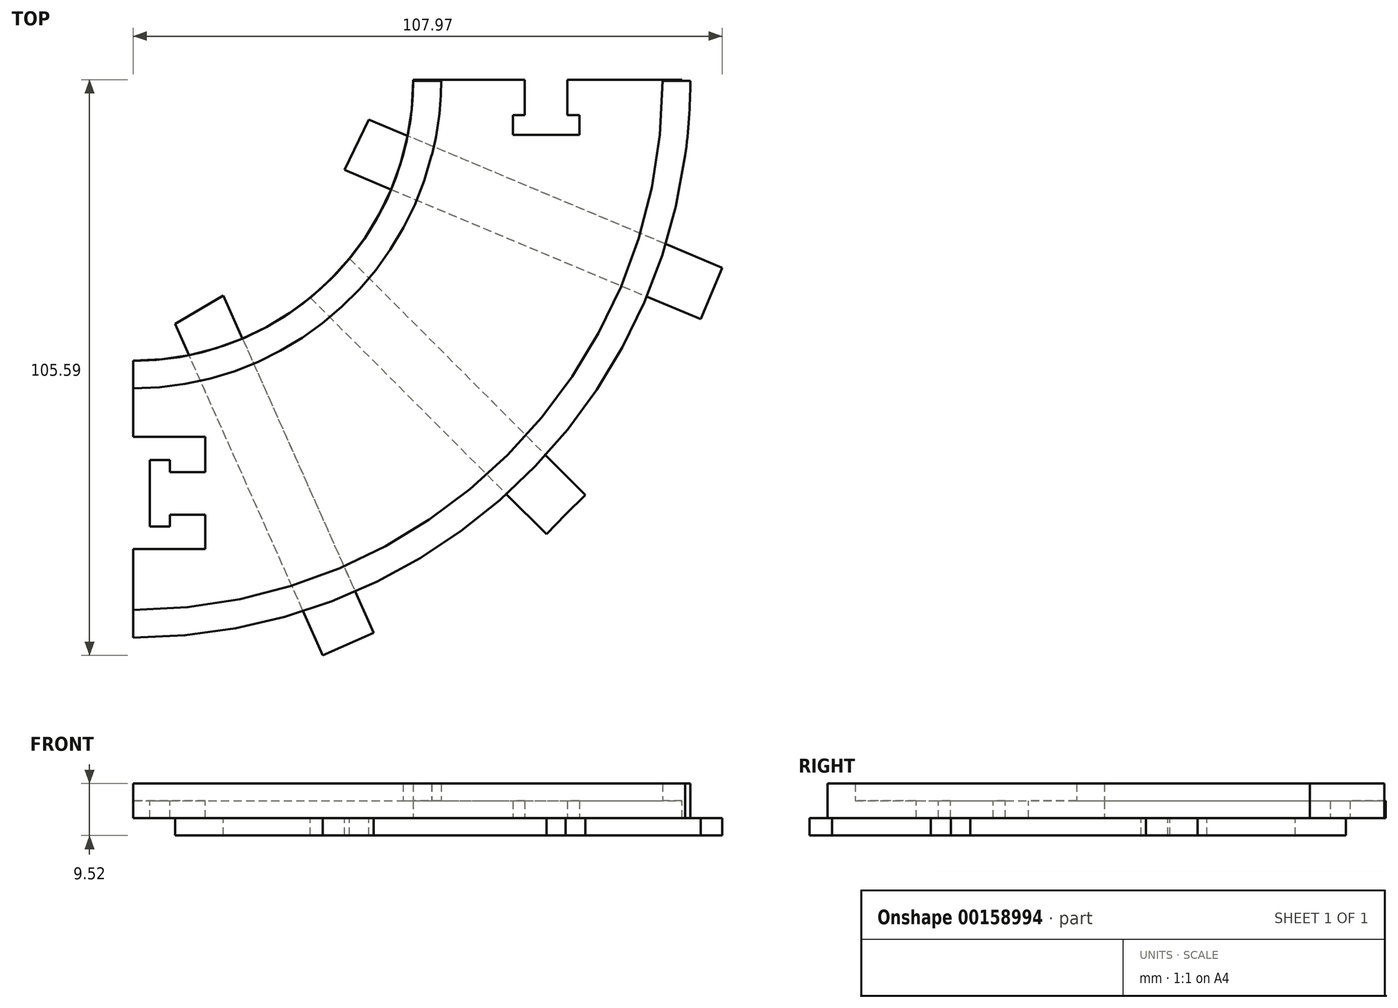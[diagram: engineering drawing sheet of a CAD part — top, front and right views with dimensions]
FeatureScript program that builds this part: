
annotation { "Feature Type Name" : "Feature", "Feature Type Description" : "" }
export const myFeature = defineFeature(function(context is Context, id is Id, definition is map)
    precondition{}
    {
        {
            var Q0;
            Q0=qCreatedBy(makeId("Top.planeOp"),FACE);
            var sketch = newSketch(context, id + "F0", { "sketchPlane" : qUnion([Q0])});
            skCircle(sketch, "E0", {"center": v(0, 0) * mm, "radius": 102.1 * mm});
            skCircle(sketch, "E1", {"center": v(0, 0) * mm, "radius": 51.3 * mm});
            skLineSegment(sketch, "E2", {"start": v(102.1, 0) * mm, "end": v(51.24, 0) * mm});
            skLineSegment(sketch, "E3", {"start": v(0, -51.3) * mm, "end": v(0, -102.1) * mm});
            skLineSegment(sketch, "E4", {"start": v(0, -102.1) * mm, "end": v(-44.33, -102.1) * mm});
            skLineSegment(sketch, "E5", {"start": v(-44.33, -102.1) * mm, "end": v(-44.33, -51.3) * mm});
            skLineSegment(sketch, "E6", {"start": v(-44.33, -51.3) * mm, "end": v(0, -51.3) * mm});
            skLineSegment(sketch, "E7", {"start": v(-16.74, -51.3) * mm, "end": v(-16.74, -102.1) * mm});
            skSolve(sketch);
        }
        {
            var Q0;
            {var subQ3=sQuery(id+"F0.wireOp",EDGE,"E3");Q0=makeQuery(id+"F0.imprint","IMPRINT",FACE,{"disambiguationData":[TD([[makeQuery(id+"F0.imprint","IMPRINT",EDGE,{"derivedFrom":subQ3}),1.0]])]});}
            extrude(context, id + "F1", {"entities" : qUnion([Q0]), "depth" : 3.17 * mm});
        }
        {
            var Q0;
            Q0=qCreatedBy(makeId("Top.planeOp"),FACE);
            var sketch = newSketch(context, id + "F2", { "sketchPlane" : qUnion([Q0])});
            skLineSegment(sketch, "E8", {"start": v(79.58, -6.3) * mm, "end": v(81.79, -6.3) * mm});
            skLineSegment(sketch, "E9", {"start": v(81.79, -6.3) * mm, "end": v(81.79, -9.91) * mm});
            skLineSegment(sketch, "E10", {"start": v(81.79, -9.91) * mm, "end": v(69.58, -9.91) * mm});
            skLineSegment(sketch, "E11", {"start": v(69.58, -9.91) * mm, "end": v(69.58, -6.3) * mm});
            skLineSegment(sketch, "E12", {"start": v(69.58, -6.3) * mm, "end": v(71.79, -6.3) * mm});
            skLineSegment(sketch, "E13", {"start": v(65.39, 0.24) * mm, "end": v(65.39, -13.41) * mm});
            skLineSegment(sketch, "E14", {"start": v(75.68, -13.41) * mm, "end": v(65.39, -13.41) * mm});
            skLineSegment(sketch, "E15", {"start": v(85.96, -13.41) * mm, "end": v(75.68, -13.41) * mm});
            skLineSegment(sketch, "E16", {"start": v(85.96, -13.41) * mm, "end": v(85.9, 0.24) * mm});
            skLineSegment(sketch, "E17", {"start": v(85.9, 0.24) * mm, "end": v(65.39, 0.24) * mm});
            skLineSegment(sketch, "E18", {"start": v(71.79, -6.3) * mm, "end": v(71.79, 0.24) * mm});
            skLineSegment(sketch, "E19", {"start": v(79.58, -6.3) * mm, "end": v(79.58, 0.24) * mm});
            skLineSegment(sketch, "E20", {"start": v(85.9, 0.24) * mm, "end": v(100.59, 0.24) * mm});
            skLineSegment(sketch, "E21", {"start": v(100.59, 0.24) * mm, "end": v(100.59, -13.41) * mm});
            skLineSegment(sketch, "E22", {"start": v(100.59, -13.41) * mm, "end": v(85.96, -13.41) * mm});
            skLineSegment(sketch, "E23", {"start": v(101.17, 0) * mm, "end": v(101.17, 0) * mm});
            skLineSegment(sketch, "E24", {"start": v(-6.04, -13.67) * mm, "end": v(65.39, -13.41) * mm});
            skLineSegment(sketch, "E25", {"start": v(51.3, -27.3) * mm, "end": v(51.3, 0.24) * mm});
            skLineSegment(sketch, "E26", {"start": v(51.3, 0.24) * mm, "end": v(65.39, 0.24) * mm});
            skLineSegment(sketch, "E27", {"start": v(100.59, 0.24) * mm, "end": v(104.76, 0.24) * mm});
            skLineSegment(sketch, "E28", {"start": v(104.76, 0.24) * mm, "end": v(104.76, -13.41) * mm});
            skLineSegment(sketch, "E29", {"start": v(104.76, -13.41) * mm, "end": v(100.59, -13.41) * mm});
            skSolve(sketch);
        }
        {
            var Q0;
            Q0=makeQuery(id+"FCGjtFl4DsFHXbu_1.boolean.opBoolean","MERGE",FACE,{"derivedFrom":[makeQuery(id+"F1.opExtrude","CAP_FACE",FACE,{"disambiguationData":[OSD([sQuery(id+"F0.wireOp",EDGE,"E0"),sQuery(id+"F0.wireOp",EDGE,"E1"),sQuery(id+"F0.wireOp",EDGE,"E2"),sQuery(id+"F0.wireOp",EDGE,"E3")])],"isStart":false}),makeQuery(id+"FCGjtFl4DsFHXbu_1.opExtrude","CAP_FACE",FACE,{"disambiguationData":[OSD([sQuery(id+"F2.wireOp",EDGE,"E8"),sQuery(id+"F2.wireOp",EDGE,"E9"),sQuery(id+"F2.wireOp",EDGE,"E10"),sQuery(id+"F2.wireOp",EDGE,"E11"),sQuery(id+"F2.wireOp",EDGE,"E12"),sQuery(id+"F2.wireOp",EDGE,"E17"),sQuery(id+"F2.wireOp",EDGE,"E18"),sQuery(id+"F2.wireOp",EDGE,"E19")])],"isStart":false}),makeQuery(id+"FCGjtFl4DsFHXbu_1.opExtrude","CAP_FACE",FACE,{"disambiguationData":[OSD([sQuery(id+"F2.wireOp",EDGE,"E13"),sQuery(id+"F2.wireOp",EDGE,"HhnOl6Ur-7oBW-enPF-9H80-fVUDD1N4fKMp"),sQuery(id+"F2.wireOp",EDGE,"E23"),sQuery(id+"F2.wireOp",EDGE,"E24")])],"isStart":false}),makeQuery(id+"FCGjtFl4DsFHXbu_1.opExtrude","CAP_FACE",FACE,{"disambiguationData":[OSD([sQuery(id+"F2.wireOp",EDGE,"E16"),sQuery(id+"F2.wireOp",EDGE,"E20"),sQuery(id+"F2.wireOp",EDGE,"E21"),sQuery(id+"F2.wireOp",EDGE,"E22")])],"isStart":false})]});
            var sketch = newSketch(context, id + "F3", { "sketchPlane" : qUnion([Q0])});
            skCircle(sketch, "E30", {"center": v(0, 0) * mm, "radius": 56.38 * mm});
            skCircle(sketch, "E31", {"center": v(0, 0) * mm, "radius": 97.01 * mm});
            skCircle(sketch, "E32", {"center": v(0, 0) * mm, "radius": 51.33 * mm});
            skCircle(sketch, "E33", {"center": v(0, 0) * mm, "radius": 102.28 * mm});
            skLineSegment(sketch, "E34", {"start": v(0, 0) * mm, "end": v(0, -102.1) * mm});
            skLineSegment(sketch, "E35", {"start": v(0, 0) * mm, "end": v(102.1, 0) * mm});
            skSolve(sketch);
        }
        {
            var Q0;
            {var subQ0=sQuery(id+"F3.wireOp",EDGE,"E35");var subQ1=sQuery(id+"F3.wireOp",EDGE,"E30");var subQ2=makeQuery(id+"F3.imprint","INTERSECT",VERTEX,{"derivedFrom":[subQ1,subQ0]});Q0=makeQuery(id+"F3.imprint","IMPRINT",FACE,{"disambiguationData":[TD([[makeQuery(id+"F3.imprint","IMPRINT",EDGE,{"disambiguationData":[TD([[subQ2,1.0]])],"derivedFrom":subQ1}),1.0]])]});}
            var Q1;
            {var subQ4=makeQuery(id+"F1.opExtrude","CAP_EDGE",EDGE,{"disambiguationData":[OSD([sQuery(id+"F0.wireOp",EDGE,"E0")])],"isStart":false});Q1=makeQuery(id+"F3.imprint","IMPRINT",FACE,{"disambiguationData":[TD([[makeQuery(id+"F3.imprint","IMPRINT",EDGE,{"derivedFrom":subQ4}),1.0]])]});}
            extrude(context, id + "F4", {"entities" : qUnion([Q0, Q1]), "operationType" : NewBodyOperationType.ADD, "depth" : 3.17 * mm});
        }
        {
            var Q0;
            Q0=qCreatedBy(makeId("Top.planeOp"),FACE);
            var sketch = newSketch(context, id + "F5", { "sketchPlane" : qUnion([Q0])});
            skCircle(sketch, "E36", {"center": v(0, 0) * mm, "radius": 56.44 * mm});
            skCircle(sketch, "E37", {"center": v(0, 0) * mm, "radius": 51.3 * mm});
            skCircle(sketch, "E38", {"center": v(0, 0) * mm, "radius": 102.1 * mm});
            skCircle(sketch, "E39", {"center": v(0, 0) * mm, "radius": 97.14 * mm});
            skLineSegment(sketch, "E40", {"start": v(0, 0) * mm, "end": v(102.1, 0) * mm});
            skLineSegment(sketch, "E41", {"start": v(0, 0) * mm, "end": v(0, -102.1) * mm});
            skLineSegment(sketch, "E42", {"start": v(49.45, -13.66) * mm, "end": v(101.19, -13.66) * mm});
            skSolve(sketch);
        }
        {
            var Q0;
            {var subQ0=sQuery(id+"F5.wireOp",EDGE,"E40");var subQ1=sQuery(id+"F5.wireOp",EDGE,"E36");var subQ2=makeQuery(id+"F5.imprint","INTERSECT",VERTEX,{"derivedFrom":[subQ1,subQ0]});Q0=makeQuery(id+"F5.imprint","IMPRINT",FACE,{"disambiguationData":[TD([[makeQuery(id+"F5.imprint","IMPRINT",EDGE,{"disambiguationData":[TD([[subQ2,1.0]])],"derivedFrom":subQ1}),1.0]])]});}
            var Q1;
            {var subQ0=sQuery(id+"F5.wireOp",EDGE,"E40");var subQ1=sQuery(id+"F5.wireOp",EDGE,"E38");var subQ2=makeQuery(id+"F5.imprint","INTERSECT",VERTEX,{"derivedFrom":[subQ1,subQ0]});Q1=makeQuery(id+"F5.imprint","IMPRINT",FACE,{"disambiguationData":[TD([[makeQuery(id+"F5.imprint","IMPRINT",EDGE,{"disambiguationData":[TD([[subQ2,1.0]])],"derivedFrom":subQ1}),1.0]])]});}
            extrude(context, id + "F6", {"entities" : qUnion([Q0, Q1]), "operationType" : NewBodyOperationType.ADD, "depth" : 6.35 * mm});
        }
        {
            var Q0;
            Q0=makeQuery(id+"F2.imprint","IMPRINT",FACE,{"disambiguationData":[TD([[makeQuery(id+"F2.imprint","IMPRINT",EDGE,{"derivedFrom":sQuery(id+"F2.wireOp",EDGE,"E13")}),-1.0]])]});
            var Q1;
            Q1=makeQuery(id+"F2.imprint","IMPRINT",FACE,{"disambiguationData":[TD([[makeQuery(id+"F2.imprint","IMPRINT",EDGE,{"derivedFrom":sQuery(id+"F2.wireOp",EDGE,"E16")}),-1.0]])]});
            extrude(context, id + "F7", {"entities" : qUnion([Q0, Q1]), "operationType" : NewBodyOperationType.ADD, "depth" : 3.17 * mm});
        }
        {
            var Q0;
            {var subQ1=sQuery(id+"F3.wireOp",EDGE,"E30");var subQ2=sQuery(id+"F0.wireOp",EDGE,"E3");var subQ5=sQuery(id+"F0.wireOp",EDGE,"E2");var subQ7=sQuery(id+"F0.wireOp",EDGE,"E0");Q0=makeQuery(id+"F7.boolean.opBoolean","MERGE",FACE,{"derivedFrom":[makeQuery(id+"F4.boolean.opBoolean","SPLIT",FACE,{"disambiguationData":[TD([makeQuery(id+"F4.opExtrude","SWEPT_FACE",FACE,{"disambiguationData":[OSD([subQ1])]})])],"derivedFrom":makeQuery(id+"F1.opExtrude","CAP_FACE",FACE,{"disambiguationData":[OSD([subQ7,sQuery(id+"F0.wireOp",EDGE,"E1"),subQ5,subQ2])],"isStart":false})}),makeQuery(id+"F7.opExtrude","CAP_FACE",FACE,{"disambiguationData":[OSD([sQuery(id+"F2.wireOp",EDGE,"E13"),sQuery(id+"F2.wireOp",EDGE,"E24"),sQuery(id+"F2.wireOp",EDGE,"E25"),sQuery(id+"F2.wireOp",EDGE,"E26")])],"isStart":false}),makeQuery(id+"F7.opExtrude","CAP_FACE",FACE,{"disambiguationData":[OSD([sQuery(id+"F2.wireOp",EDGE,"E16"),sQuery(id+"F2.wireOp",EDGE,"E20"),sQuery(id+"F2.wireOp",EDGE,"E21"),sQuery(id+"F2.wireOp",EDGE,"E22")])],"isStart":false})]});}
            var sketch = newSketch(context, id + "F8", { "sketchPlane" : qUnion([Q0])});
            skLineSegment(sketch, "E43.top", {"start": v(13.23, -101.1) * mm, "end": v(13.23, -50.3) * mm});
            skLineSegment(sketch, "E44", {"start": v(13.23, -86) * mm, "end": v(13.23, -79.51) * mm});
            skLineSegment(sketch, "E45", {"start": v(13.23, -79.51) * mm, "end": v(6.76, -79.51) * mm});
            skLineSegment(sketch, "E46", {"start": v(6.76, -79.51) * mm, "end": v(6.76, -81.72) * mm});
            skLineSegment(sketch, "E47", {"start": v(6.76, -81.72) * mm, "end": v(3.06, -81.72) * mm});
            skLineSegment(sketch, "E48", {"start": v(3.06, -81.72) * mm, "end": v(3.06, -69.51) * mm});
            skLineSegment(sketch, "E49", {"start": v(3.06, -69.51) * mm, "end": v(6.76, -69.51) * mm});
            skLineSegment(sketch, "E50", {"start": v(6.76, -69.51) * mm, "end": v(6.76, -71.72) * mm});
            skLineSegment(sketch, "E51", {"start": v(6.76, -71.72) * mm, "end": v(13.23, -71.72) * mm});
            skLineSegment(sketch, "E52", {"start": v(13.23, -71.72) * mm, "end": v(13.23, -65.25) * mm});
            skLineSegment(sketch, "E53", {"start": v(13.23, -65.25) * mm, "end": v(-0.42, -65.25) * mm});
            skLineSegment(sketch, "E54", {"start": v(-0.42, -75.54) * mm, "end": v(-0.42, -65.25) * mm});
            skLineSegment(sketch, "E55", {"start": v(-0.42, -85.83) * mm, "end": v(-0.42, -75.54) * mm});
            skLineSegment(sketch, "E56", {"start": v(-0.42, -85.83) * mm, "end": v(13.23, -85.83) * mm});
            skLineSegment(sketch, "E57", {"start": v(13.23, -85.83) * mm, "end": v(13.23, -65.25) * mm});
            skLineSegment(sketch, "E58", {"start": v(-0.42, -85.83) * mm, "end": v(-0.42, -101.1) * mm});
            skLineSegment(sketch, "E59", {"start": v(-0.42, -101.1) * mm, "end": v(-0.42, -65.25) * mm});
            skLineSegment(sketch, "E60", {"start": v(-0.42, -65.25) * mm, "end": v(-0.42, -50.3) * mm});
            skLineSegment(sketch, "E61", {"start": v(-0.42, -101.1) * mm, "end": v(13.23, -101.1) * mm});
            skLineSegment(sketch, "E62", {"start": v(-0.42, -50.3) * mm, "end": v(13.23, -50.3) * mm});
            skSolve(sketch);
        }
        {
            var Q0;
            {var subQ10=sQuery(id+"F8.wireOp",EDGE,"E45");Q0=makeQuery(id+"F8.imprint","IMPRINT",FACE,{"disambiguationData":[TD([[makeQuery(id+"F8.imprint","IMPRINT",EDGE,{"derivedFrom":subQ10}),1.0]])]});}
            extrude(context, id + "F9", {"entities" : qUnion([Q0]), "operationType" : NewBodyOperationType.REMOVE, "oppositeDirection" : true, "depth" : 25.4 * mm});
        }
        {
            var Q0;
            {var subQ0=sQuery(id+"F5.wireOp",EDGE,"E42");var subQ1=sQuery(id+"F5.wireOp",EDGE,"E40");Q0=makeQuery(id+"F7.boolean.opBoolean","MERGE",FACE,{"derivedFrom":[makeQuery(id+"F6.boolean.opBoolean","MERGE",FACE,{"derivedFrom":[makeQuery(id+"F1.opExtrude","CAP_FACE",FACE,{"disambiguationData":[OSD([sQuery(id+"F0.wireOp",EDGE,"E0"),sQuery(id+"F0.wireOp",EDGE,"E1"),sQuery(id+"F0.wireOp",EDGE,"E2"),sQuery(id+"F0.wireOp",EDGE,"E3")])],"isStart":true}),makeQuery(id+"F6.opExtrude","CAP_FACE",FACE,{"disambiguationData":[OSD([sQuery(id+"F5.wireOp",EDGE,"E36"),sQuery(id+"F5.wireOp",EDGE,"E37"),subQ1,subQ0])],"isStart":true}),makeQuery(id+"F6.opExtrude","CAP_FACE",FACE,{"disambiguationData":[OSD([sQuery(id+"F5.wireOp",EDGE,"E38"),sQuery(id+"F5.wireOp",EDGE,"E39"),subQ1,subQ0])],"isStart":true})]}),makeQuery(id+"F7.opExtrude","CAP_FACE",FACE,{"disambiguationData":[OSD([sQuery(id+"F2.wireOp",EDGE,"E13"),sQuery(id+"F2.wireOp",EDGE,"E24"),sQuery(id+"F2.wireOp",EDGE,"E25"),sQuery(id+"F2.wireOp",EDGE,"E26")])],"isStart":true}),makeQuery(id+"F7.opExtrude","CAP_FACE",FACE,{"disambiguationData":[OSD([sQuery(id+"F2.wireOp",EDGE,"E16"),sQuery(id+"F2.wireOp",EDGE,"E20"),sQuery(id+"F2.wireOp",EDGE,"E21"),sQuery(id+"F2.wireOp",EDGE,"E22")])],"isStart":true})]});}
            var sketch = newSketch(context, id + "F10", { "sketchPlane" : qUnion([Q0])});
            skLineSegment(sketch, "E63", {"start": v(72.1, 72.28) * mm, "end": v(0, 0) * mm});
            skLineSegment(sketch, "E64", {"start": v(72.1, 72.28) * mm, "end": v(79.27, 79.48) * mm});
            skLineSegment(sketch, "E65", {"start": v(36.22, 36.32) * mm, "end": v(29.05, 29.12) * mm});
            skLineSegment(sketch, "E66", {"start": v(29.05, 29.12) * mm, "end": v(25.45, 32.71) * mm});
            skLineSegment(sketch, "E67", {"start": v(29.05, 29.12) * mm, "end": v(32.65, 25.54) * mm});
            skLineSegment(sketch, "E68", {"start": v(25.45, 32.71) * mm, "end": v(75.73, 83.12) * mm});
            skLineSegment(sketch, "E69", {"start": v(75.73, 83.12) * mm, "end": v(79.27, 79.48) * mm});
            skLineSegment(sketch, "E70", {"start": v(32.65, 25.54) * mm, "end": v(82.88, 75.9) * mm});
            skLineSegment(sketch, "E71", {"start": v(82.88, 75.9) * mm, "end": v(79.27, 79.48) * mm});
            skLineSegment(sketch, "E72", {"start": v(25.45, 32.71) * mm, "end": v(16.52, 39.32) * mm});
            skLineSegment(sketch, "E73", {"start": v(32.65, 25.54) * mm, "end": v(38.71, 16.31) * mm});
            skLineSegment(sketch, "E74", {"start": v(38.71, 16.31) * mm, "end": v(104.01, 43.7) * mm});
            skLineSegment(sketch, "E75", {"start": v(104.01, 43.7) * mm, "end": v(107.97, 34.26) * mm});
            skLineSegment(sketch, "E76", {"start": v(107.97, 34.26) * mm, "end": v(43.16, 7.08) * mm});
            skLineSegment(sketch, "E77", {"start": v(43.16, 7.08) * mm, "end": v(38.71, 16.31) * mm});
            skLineSegment(sketch, "E78", {"start": v(16.52, 39.32) * mm, "end": v(44.06, 101.21) * mm});
            skLineSegment(sketch, "E79", {"start": v(44.06, 101.21) * mm, "end": v(34.76, 105.35) * mm});
            skLineSegment(sketch, "E80", {"start": v(34.76, 105.35) * mm, "end": v(7.71, 44.58) * mm});
            skLineSegment(sketch, "E81", {"start": v(7.71, 44.58) * mm, "end": v(16.52, 39.32) * mm});
            skSolve(sketch);
        }
        {
            var Q0;
            {var subQ0=sQuery(id+"F10.wireOp",EDGE,"E65");Q0=makeQuery(id+"F10.imprint","IMPRINT",FACE,{"disambiguationData":[TD([[makeQuery(id+"F10.imprint","IMPRINT",EDGE,{"derivedFrom":subQ0}),1.0]])]});}
            var Q1;
            {var subQ0=sQuery(id+"F10.wireOp",EDGE,"E65");Q1=makeQuery(id+"F10.imprint","IMPRINT",FACE,{"disambiguationData":[TD([[makeQuery(id+"F10.imprint","IMPRINT",EDGE,{"derivedFrom":subQ0}),-1.0]])]});}
            var Q2;
            {var subQ1=makeQuery(id+"F1.opExtrude","CAP_EDGE",EDGE,{"disambiguationData":[OSD([sQuery(id+"F0.wireOp",EDGE,"E0")])],"isStart":true});var subQ5=sQuery(id+"F10.wireOp",EDGE,"E68");var subQ6=makeQuery(id+"F10.imprint","INTERSECT",VERTEX,{"derivedFrom":[subQ1,subQ5]});Q2=makeQuery(id+"F10.imprint","IMPRINT",FACE,{"disambiguationData":[TD([[makeQuery(id+"F10.imprint","IMPRINT",EDGE,{"disambiguationData":[TD([[subQ6,1.0]])],"derivedFrom":subQ5}),-1.0]])]});}
            var Q3;
            {var subQ1=makeQuery(id+"F1.opExtrude","CAP_EDGE",EDGE,{"disambiguationData":[OSD([sQuery(id+"F0.wireOp",EDGE,"E0")])],"isStart":true});var subQ5=sQuery(id+"F10.wireOp",EDGE,"E70");var subQ6=makeQuery(id+"F10.imprint","INTERSECT",VERTEX,{"derivedFrom":[subQ1,subQ5]});Q3=makeQuery(id+"F10.imprint","IMPRINT",FACE,{"disambiguationData":[TD([[makeQuery(id+"F10.imprint","IMPRINT",EDGE,{"disambiguationData":[TD([[subQ6,1.0]])],"derivedFrom":subQ5}),1.0]])]});}
            var Q4;
            {var subQ0=sQuery(id+"F10.wireOp",EDGE,"E64");Q4=makeQuery(id+"F10.imprint","IMPRINT",FACE,{"disambiguationData":[TD([[makeQuery(id+"F10.imprint","IMPRINT",EDGE,{"derivedFrom":subQ0}),-1.0]])]});}
            var Q5;
            {var subQ0=sQuery(id+"F10.wireOp",EDGE,"E64");Q5=makeQuery(id+"F10.imprint","IMPRINT",FACE,{"disambiguationData":[TD([[makeQuery(id+"F10.imprint","IMPRINT",EDGE,{"derivedFrom":subQ0}),1.0]])]});}
            var Q6;
            {var subQ0=sQuery(id+"F10.wireOp",EDGE,"E78");var subQ1=makeQuery(id+"F1.opExtrude","CAP_EDGE",EDGE,{"disambiguationData":[OSD([sQuery(id+"F0.wireOp",EDGE,"E0")])],"isStart":true});var subQ2=makeQuery(id+"F10.imprint","INTERSECT",VERTEX,{"derivedFrom":[subQ1,subQ0]});Q6=makeQuery(id+"F10.imprint","IMPRINT",FACE,{"disambiguationData":[TD([[makeQuery(id+"F10.imprint","IMPRINT",EDGE,{"disambiguationData":[TD([[subQ2,1.0]])],"derivedFrom":subQ0}),1.0]])]});}
            var Q7;
            {var subQ0=sQuery(id+"F10.wireOp",EDGE,"E79");Q7=makeQuery(id+"F10.imprint","IMPRINT",FACE,{"disambiguationData":[TD([[makeQuery(id+"F10.imprint","IMPRINT",EDGE,{"derivedFrom":subQ0}),1.0]])]});}
            var Q8;
            {var subQ0=sQuery(id+"F10.wireOp",EDGE,"E81");Q8=makeQuery(id+"F10.imprint","IMPRINT",FACE,{"disambiguationData":[TD([[makeQuery(id+"F10.imprint","IMPRINT",EDGE,{"derivedFrom":subQ0}),1.0]])]});}
            var Q9;
            {var subQ8=sQuery(id+"F10.wireOp",EDGE,"E77");Q9=makeQuery(id+"F10.imprint","IMPRINT",FACE,{"disambiguationData":[TD([[makeQuery(id+"F10.imprint","IMPRINT",EDGE,{"derivedFrom":subQ8}),-1.0]])]});}
            var Q10;
            {var subQ7=sQuery(id+"F0.wireOp",EDGE,"E0");var subQ10=sQuery(id+"F10.wireOp",EDGE,"E74");var subQ13=makeQuery(id+"F1.opExtrude","CAP_EDGE",EDGE,{"disambiguationData":[OSD([subQ7])],"isStart":true});var subQ17=makeQuery(id+"F10.imprint","INTERSECT",VERTEX,{"derivedFrom":[subQ13,subQ10]});Q10=makeQuery(id+"F10.imprint","IMPRINT",FACE,{"disambiguationData":[TD([[makeQuery(id+"F10.imprint","IMPRINT",EDGE,{"disambiguationData":[TD([[subQ17,1.0]])],"derivedFrom":subQ10}),-1.0]])]});}
            var Q11;
            {var subQ0=sQuery(id+"F10.wireOp",EDGE,"E75");Q11=makeQuery(id+"F10.imprint","IMPRINT",FACE,{"disambiguationData":[TD([[makeQuery(id+"F10.imprint","IMPRINT",EDGE,{"derivedFrom":subQ0}),-1.0]])]});}
            extrude(context, id + "F11", {"entities" : qUnion([Q0, Q1, Q2, Q3, Q4, Q5, Q6, Q7, Q8, Q9, Q10, Q11]), "operationType" : NewBodyOperationType.ADD, "depth" : 3.17 * mm});
        }
        {
            var Q0;
            {var subQ0=sQuery(id+"F5.wireOp",EDGE,"E42");var subQ1=sQuery(id+"F5.wireOp",EDGE,"E38");var subQ2=sQuery(id+"F5.wireOp",EDGE,"E39");var subQ3=sQuery(id+"F0.wireOp",EDGE,"E0");var subQ6=sQuery(id+"F5.wireOp",EDGE,"E40");var subQ7=sQuery(id+"F0.wireOp",EDGE,"E2");var subQ8=makeQuery(id+"F1.opExtrude","SWEPT_FACE",FACE,{"disambiguationData":[OSD([subQ7])]});var subQ9=sQuery(id+"F2.wireOp",EDGE,"E13");var subQ10=sQuery(id+"F2.wireOp",EDGE,"E22");var subQ12=sQuery(id+"F2.wireOp",EDGE,"E20");var subQ17=makeQuery(id+"F1.opExtrude","SWEPT_FACE",FACE,{"disambiguationData":[OSD([subQ3])]});var subQ18=sQuery(id+"F0.wireOp",EDGE,"E1");var subQ23=sQuery(id+"F2.wireOp",EDGE,"E16");var subQ24=sQuery(id+"F2.wireOp",EDGE,"E21");var subQ25=sQuery(id+"F2.wireOp",EDGE,"E25");var subQ26=sQuery(id+"F2.wireOp",EDGE,"E26");var subQ27=sQuery(id+"F2.wireOp",EDGE,"E24");var subQ29=sQuery(id+"F0.wireOp",EDGE,"E3");Q0=makeQuery(id+"F11.boolean.opBoolean","SPLIT",FACE,{"disambiguationData":[TD([subQ8])],"derivedFrom":makeQuery(id+"F7.boolean.opBoolean","MERGE",FACE,{"derivedFrom":[makeQuery(id+"F6.boolean.opBoolean","MERGE",FACE,{"derivedFrom":[makeQuery(id+"Fei38nU6vnmVDr2_1.boolean.opBoolean","SPLIT",FACE,{"disambiguationData":[TD([subQ17])],"derivedFrom":makeQuery(id+"F1.opExtrude","CAP_FACE",FACE,{"disambiguationData":[OSD([subQ3,subQ18,subQ7,subQ29])],"isStart":true})}),makeQuery(id+"F6.opExtrude","CAP_FACE",FACE,{"disambiguationData":[OSD([sQuery(id+"F5.wireOp",EDGE,"E36"),sQuery(id+"F5.wireOp",EDGE,"E37"),subQ6,subQ0])],"isStart":true}),makeQuery(id+"F6.opExtrude","CAP_FACE",FACE,{"disambiguationData":[OSD([subQ1,subQ2,subQ6,subQ0])],"isStart":true})]}),makeQuery(id+"F7.opExtrude","CAP_FACE",FACE,{"disambiguationData":[OSD([subQ9,subQ27,subQ25,subQ26])],"isStart":true}),makeQuery(id+"F7.opExtrude","CAP_FACE",FACE,{"disambiguationData":[OSD([subQ23,subQ12,subQ24,subQ10])],"isStart":true})]})});}
            var sketch = newSketch(context, id + "F12", { "sketchPlane" : qUnion([Q0])});
            skLineSegment(sketch, "E82", {"start": v(65.39, -0.24) * mm, "end": v(85.9, -0.24) * mm});
            skSolve(sketch);
        }
        {
            var Q0;
            Q0=makeQuery(id+"F12.imprint","IMPRINT",FACE,{"disambiguationData":[TD([[makeQuery(id+"F12.imprint","IMPRINT",EDGE,{"derivedFrom":sQuery(id+"F12.wireOp",EDGE,"E82")}),1.0]])]});
            extrude(context, id + "F13", {"entities" : qUnion([Q0]), "operationType" : NewBodyOperationType.ADD, "oppositeDirection" : true, "depth" : 3.17 * mm});
        }
        {
            var Q0;
            Q0=makeQuery(id+"F2.imprint","IMPRINT",FACE,{"disambiguationData":[TD([[makeQuery(id+"F2.imprint","IMPRINT",EDGE,{"derivedFrom":sQuery(id+"F2.wireOp",EDGE,"E8")}),-1.0]])]});
            extrude(context, id + "F14", {"entities" : qUnion([Q0]), "operationType" : NewBodyOperationType.REMOVE, "depth" : 25.4 * mm});
        }
    });
